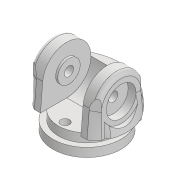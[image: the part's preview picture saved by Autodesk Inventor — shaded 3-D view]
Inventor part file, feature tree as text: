
AUTODESK INVENTOR PART (.ipt)
format: ipt  version: 2020 (Build 240168000, 168)  size: 818,688 bytes
history: native  units: mm
features: sketch x19, extrude x16, projected_geometry x4, mirror x3, loft x2, plane x2, other x2, fillet x1
ambient origin geometry x8: Origin, YZ Plane, XZ Plane, XY Plane, X Axis, Y Axis, Z Axis, Center Point
bodies: Solid1 (feature_tree)
feature tree (49):
  extrude  "Extrusion1"  Depth=2.0mm TaperAngle=0.0deg
  extrude  "Extrusion2"  Depth=2.0mm TaperAngle=0.0deg
  extrude  "Extrusion3"  Depth=11.0mm
  loft  "Loft1"
  sketch  "Sketch6"  dims[d58=-5.5mm d59=0.0mm]
  plane  "Work Plane1"
  loft  "Loft2"
  extrude  "Extrusion4"  TaperAngle=0.0deg  [1 undecoded]
  extrude  "Extrusion5"  TaperAngle=0.0deg  [1 undecoded]
  fillet  "Fillet1"  Radius=12.0mm
  extrude  "Extrusion6"  Depth=1.0mm
  extrude  "Extrusion7"  Depth=8.75mm TaperAngle=0.0deg
  extrude  "Extrusion8"  Depth=13.0mm
  extrude  "Extrusion9"  Depth=5.1mm
  mirror  "Mirror1"
  extrude  "Extrusion10"  Depth=2.12mm
  extrude  "Extrusion11"  Depth=6.75mm
  mirror  "Mirror2"
  extrude  "Extrusion12"  Depth=8.8mm
  mirror  "Mirror3"
  extrude  "Extrusion13"  Depth=11.0mm
  extrude  "Extrusion17"  Depth=2.1mm
  extrude  "Extrusion18"  Depth=0.627mm
  extrude  "Extrusion19"  Depth=10.0mm TaperAngle=0.0deg
  sketch  "Sketch1"  dims[d0=15.5mm d1=2.0mm d2=0.0mm]
  sketch  "Sketch2"  dims[d3=12.0mm d4=2.0mm d5=0.0mm]
  sketch  "Sketch3"  dims[d6=5.5mm d7=11.0mm]
  sketch  "Sketch4"  dims[d8=12.0mm d9=0.0mm d38=0.0mm d39=90.0deg]
  other  "Image1"
  sketch  "Sketch5"  dims[d40=0.0mm d41=90.0deg d49=0.0mm]
  other  "Image2"
  projected_geometry  "Projected Loop1"
  sketch  "Sketch7"  dims[d60=0.0mm d61=90.0deg d62=0.0mm d63=90.0deg d64=12.0mm d65=0.0mm]
  projected_geometry  "Projected Loop2"
  sketch  "Sketch8"  dims[d66=7.792mm d67=0.0mm d68=1.0mm]
  projected_geometry  "Projected Loop3"
  sketch  "Sketch9"  dims[d69=4.6mm d70=8.75mm d71=5.5mm d72=0.0mm d73=0.0mm]
  projected_geometry  "Projected Loop4"
  sketch  "Sketch10"  dims[d74=4.0mm d75=0.0mm d76=13.0mm]
  sketch  "Sketch11"  dims[d77=2.0mm d78=0.0mm d79=5.1mm]
  sketch  "Sketch12"  dims[d80=0.5mm d81=0.0mm d82=2.12mm]
  sketch  "Sketch13"  dims[d83=12.236mm d84=0.0mm d85=6.75mm]
  plane  "Work Plane2"
  sketch  "Sketch14"  dims[d86=2.9mm d87=1.8mm d88=0.0mm d89=0.0mm d90=8.8mm]
  sketch  "Sketch15"  dims[d91=2.9mm d92=0.0mm d93=11.0mm]
  sketch  "Sketch16"  dims[d94=4.9mm d95=0.0mm d109=2.1mm]
  sketch  "Sketch21"  dims[d110=0.0mm d111=0.0mm d112=0.627mm]
  sketch  "Sketch22"  dims[d113=1.637mm d114=10.0mm d115=0.0mm]
  sketch  "Sketch23"  dims[d116=2.0mm d117=10.0mm d118=0.0mm]
note: 2 required parameter values undecoded (feature->parameter linkage not recoverable at this tier; creation-order binding heuristic only, values carry confidence <= 0.55)
